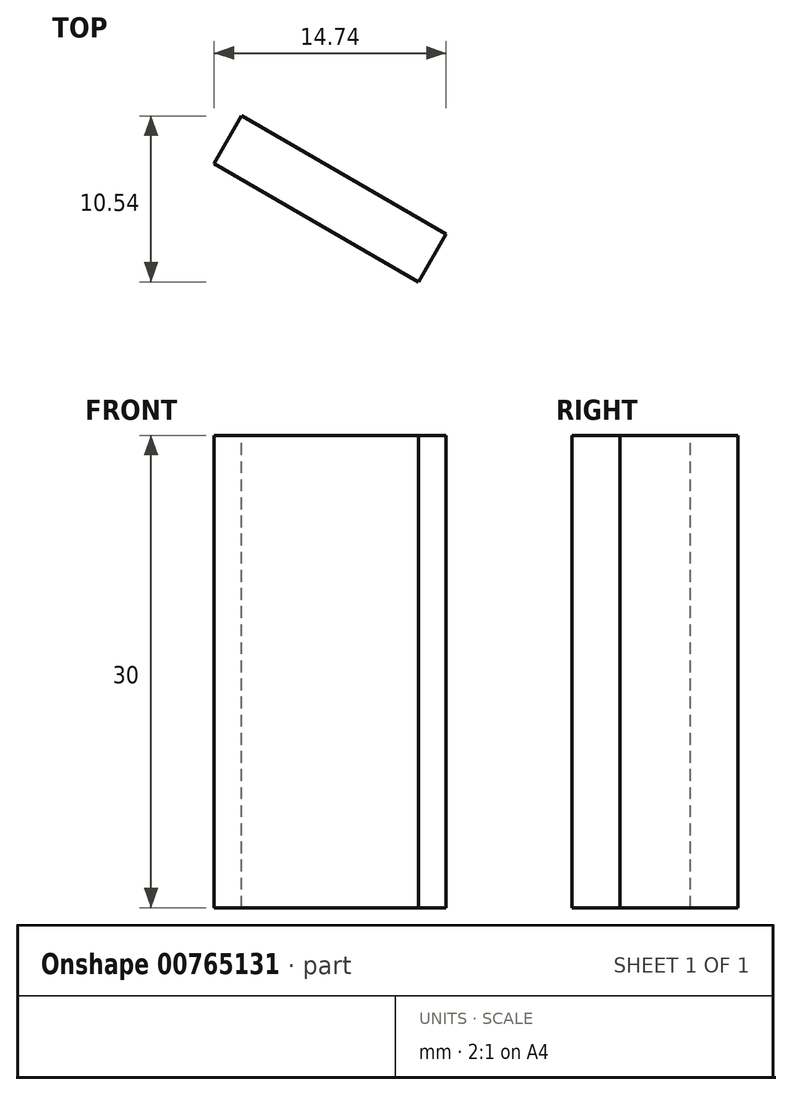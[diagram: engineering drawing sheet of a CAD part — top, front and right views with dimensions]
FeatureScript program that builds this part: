
annotation { "Feature Type Name" : "Feature", "Feature Type Description" : "" }
export const myFeature = defineFeature(function(context is Context, id is Id, definition is map)
    precondition{}
    {
        {
            var Q0;
            Q0=qCreatedBy(makeId("Top.planeOp"),FACE);
            var sketch = newSketch(context, id + "F0", { "sketchPlane" : qUnion([Q0])});
            skLineSegment(sketch, "E0.4", {"start": v(-0.02, -15) * mm, "end": v(-13, -7.48) * mm});
            skPoint(sketch, "E0.0.midPoint", {"position": v(-6.48, 11.26) * mm});
            skLineSegment(sketch, "E1.0", {"start": v(1.74, -11.97) * mm, "end": v(-11.25, -4.46) * mm});
            skLineSegment(sketch, "E2", {"start": v(1.74, -11.97) * mm, "end": v(-0.02, -15) * mm});
            skLineSegment(sketch, "E3", {"start": v(-11.25, -4.46) * mm, "end": v(-13, -7.48) * mm});
            skSolve(sketch);
        }
        {
            var Q0;
            Q0=makeQuery(id+"F0.imprint","IMPRINT",FACE,{"disambiguationData":[TD([[makeQuery(id+"F0.imprint","IMPRINT",EDGE,{"derivedFrom":sQuery(id+"F0.wireOp",EDGE,"E0.4")}),-1.0]])]});
            extrude(context, id + "F1", {"entities" : qUnion([Q0]), "oppositeDirection" : true, "depth" : 30 * mm, "offsetDistance" : 25 * mm});
        }
    });
